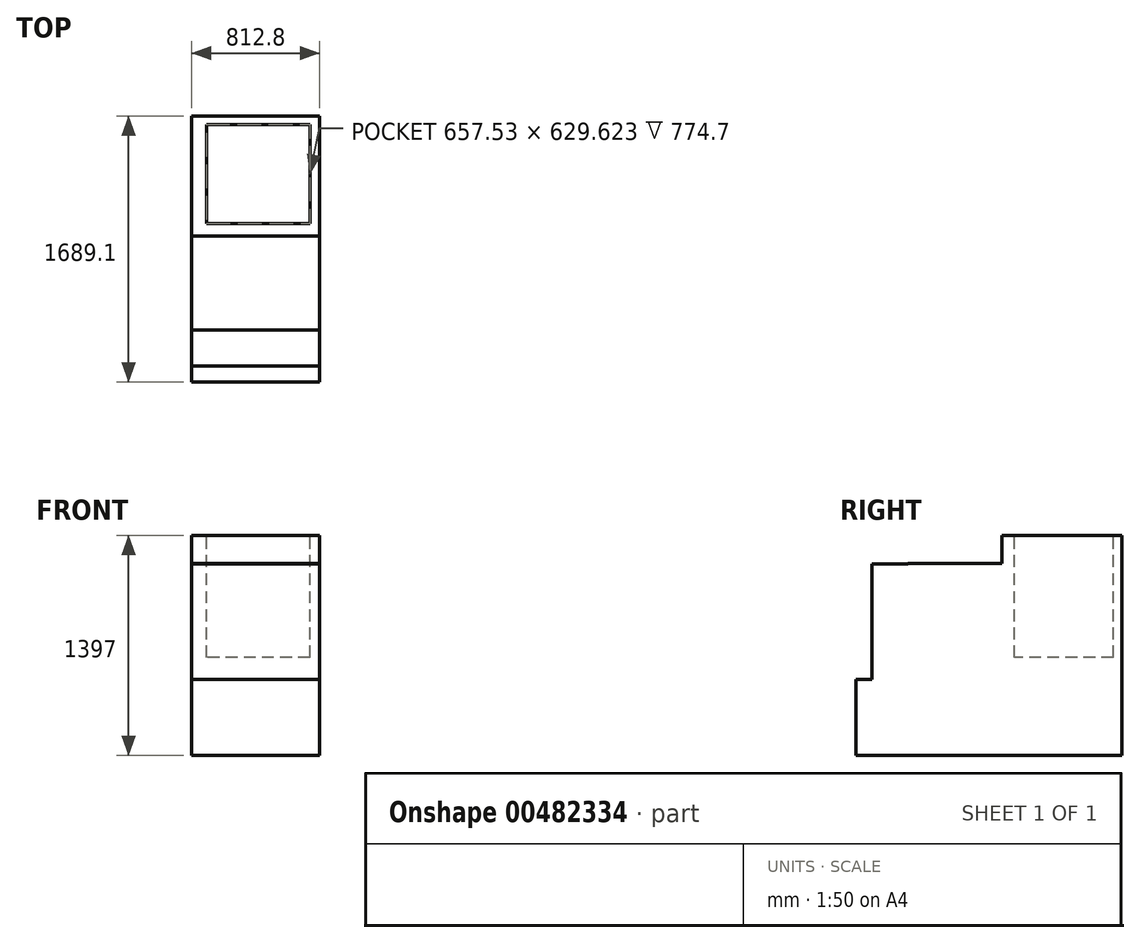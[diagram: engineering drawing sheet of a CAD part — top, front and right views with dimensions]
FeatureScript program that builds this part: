
annotation { "Feature Type Name" : "Feature", "Feature Type Description" : "" }
export const myFeature = defineFeature(function(context is Context, id is Id, definition is map)
    precondition{}
    {
        {
            var Q0;
            Q0=qCreatedBy(makeId("Top.planeOp"),FACE);
            var sketch = newSketch(context, id + "F0", { "sketchPlane" : qUnion([Q0])});
            skLineSegment(sketch, "E0.bottom", {"start": v(0, 0) * mm, "end": v(812.8, 0) * mm});
            skLineSegment(sketch, "E0.top", {"start": v(0, 101.6) * mm, "end": v(812.8, 101.6) * mm});
            skLineSegment(sketch, "E0.left", {"start": v(0, 0) * mm, "end": v(0, 101.6) * mm});
            skLineSegment(sketch, "E0.right", {"start": v(812.8, 0) * mm, "end": v(812.8, 101.6) * mm});
            skSolve(sketch);
        }
        {
            var Q0;
            Q0 = qSketchRegion(id + "F0", true);
            extrude(context, id + "F1", {"entities" : qUnion([Q0]), "depth" : 482.6 * mm, "offsetDistance" : 25.4 * mm});
        }
        {
            var Q0;
            Q0=makeQuery(id+"F1.opExtrude","CAP_FACE",FACE,{"disambiguationData":[OSD([sQuery(id+"F0.wireOp",EDGE,"E0.bottom"),sQuery(id+"F0.wireOp",EDGE,"E0.top"),sQuery(id+"F0.wireOp",EDGE,"E0.left"),sQuery(id+"F0.wireOp",EDGE,"E0.right")])],"isStart":false});
            var sketch = newSketch(context, id + "F2", { "sketchPlane" : qUnion([Q0])});
            skLineSegment(sketch, "E1.bottom", {"start": v(0, 101.6) * mm, "end": v(812.8, 101.6) * mm});
            skLineSegment(sketch, "E1.top", {"start": v(0, 330.2) * mm, "end": v(812.8, 330.2) * mm});
            skLineSegment(sketch, "E1.left", {"start": v(0, 101.6) * mm, "end": v(0, 330.2) * mm});
            skLineSegment(sketch, "E1.right", {"start": v(812.8, 101.6) * mm, "end": v(812.8, 330.2) * mm});
            skSolve(sketch);
        }
        {
            var Q0;
            Q0 = qSketchRegion(id + "F2", true);
            var Q1;
            Q1=makeQuery(id+"F1.opExtrude","CAP_FACE",FACE,{"disambiguationData":[OSD([sQuery(id+"F0.wireOp",EDGE,"E0.bottom"),sQuery(id+"F0.wireOp",EDGE,"E0.top"),sQuery(id+"F0.wireOp",EDGE,"E0.left"),sQuery(id+"F0.wireOp",EDGE,"E0.right")])],"isStart":true});
            extrude(context, id + "F3", {"entities" : qUnion([Q0]), "operationType" : NewBodyOperationType.ADD, "depth" : 734.06 * mm, "offsetDistance" : 25.4 * mm, "hasSecondDirection" : true, "secondDirectionBound" : BoundingType.UP_TO_SURFACE, "secondDirectionOppositeDirection" : true, "secondDirectionDepth" : 25.4 * mm, "secondDirectionBoundEntityFace" : qUnion([Q1])});
        }
        {
            var Q0;
            Q0=qCreatedBy(makeId("Top.planeOp"),FACE);
            var sketch = newSketch(context, id + "F4", { "sketchPlane" : qUnion([Q0])});
            skLineSegment(sketch, "E2.bottom", {"start": v(0, 927.1) * mm, "end": v(812.8, 927.1) * mm});
            skLineSegment(sketch, "E2.top", {"start": v(0, 330.2) * mm, "end": v(812.8, 330.2) * mm});
            skLineSegment(sketch, "E2.left", {"start": v(0, 927.1) * mm, "end": v(0, 330.2) * mm});
            skLineSegment(sketch, "E2.right", {"start": v(812.8, 927.1) * mm, "end": v(812.8, 330.2) * mm});
            skSolve(sketch);
        }
        {
            var Q0;
            Q0 = qSketchRegion(id + "F4", true);
            extrude(context, id + "F5", {"entities" : qUnion([Q0]), "operationType" : NewBodyOperationType.ADD, "depth" : 1219.2 * mm, "offsetDistance" : 25.4 * mm});
        }
        {
            var Q0;
            Q0=makeQuery(id+"F5.opExtrude","SWEPT_FACE",FACE,{"disambiguationData":[OSD([sQuery(id+"F4.wireOp",EDGE,"E2.bottom")])]});
            var sketch = newSketch(context, id + "F6", { "sketchPlane" : qUnion([Q0])});
            skLineSegment(sketch, "E3.bottom", {"start": v(-812.8, 0) * mm, "end": v(0, 0) * mm});
            skLineSegment(sketch, "E3.top", {"start": v(-812.8, 1397) * mm, "end": v(0, 1397) * mm});
            skLineSegment(sketch, "E3.left", {"start": v(-812.8, 0) * mm, "end": v(-812.8, 1397) * mm});
            skLineSegment(sketch, "E3.right", {"start": v(0, 0) * mm, "end": v(0, 1397) * mm});
            skSolve(sketch);
        }
        {
            var Q0;
            Q0 = qSketchRegion(id + "F6", true);
            extrude(context, id + "F7", {"entities" : qUnion([Q0]), "operationType" : NewBodyOperationType.ADD, "depth" : 762 * mm, "offsetDistance" : 25.4 * mm});
        }
        {
            var Q0;
            Q0=makeQuery(id+"F7.opExtrude","SWEPT_FACE",FACE,{"disambiguationData":[OSD([sQuery(id+"F6.wireOp",EDGE,"E3.top")])]});
            var sketch = newSketch(context, id + "F8", { "sketchPlane" : qUnion([Q0])});
            skLineSegment(sketch, "E4.bottom", {"start": v(751.88, 1635.6) * mm, "end": v(94.35, 1635.6) * mm});
            skLineSegment(sketch, "E4.top", {"start": v(751.88, 1005.98) * mm, "end": v(94.35, 1005.98) * mm});
            skLineSegment(sketch, "E4.left", {"start": v(751.88, 1635.6) * mm, "end": v(751.88, 1005.98) * mm});
            skLineSegment(sketch, "E4.right", {"start": v(94.35, 1635.6) * mm, "end": v(94.35, 1005.98) * mm});
            skSolve(sketch);
        }
        {
            var Q0;
            Q0 = qSketchRegion(id + "F8", true);
            extrude(context, id + "F9", {"entities" : qUnion([Q0]), "operationType" : NewBodyOperationType.REMOVE, "oppositeDirection" : true, "depth" : 774.7 * mm, "offsetDistance" : 25.4 * mm});
        }
    });
